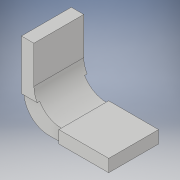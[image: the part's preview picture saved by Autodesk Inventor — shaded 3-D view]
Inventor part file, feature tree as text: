
AUTODESK INVENTOR PART (.ipt)
format: ipt  version: 2017 (Build 210142000, 142)  size: 118,272 bytes
history: native  units: in
note: dims shown in document units (in); Inventor stores cm internally (conversion verified against a paired STEP export)
features: extrude x1, pattern_circular x1, fillet x1, sketch x1
ambient origin geometry x8: Origin, YZ Plane, XZ Plane, XY Plane, X Axis, Y Axis, Z Axis, Center Point
bodies: Solid1 (feature_tree)
feature tree (4):
  extrude  "Extrusion1"  Depth=0.125in
  pattern_circular  "Circular Pattern1"  [2 undecoded]
  fillet  "Fillet1"  Radius=0.0625in
  sketch  "Sketch1"  dims[d0=0.25in d1=0.125in d2=0.225in d3=0.0625in d4=0.0in d5=0.7874in d6=90.0deg d8=0.125in]
note: 2 required parameter values undecoded (feature->parameter linkage not recoverable at this tier; creation-order binding heuristic only, values carry confidence <= 0.55)
